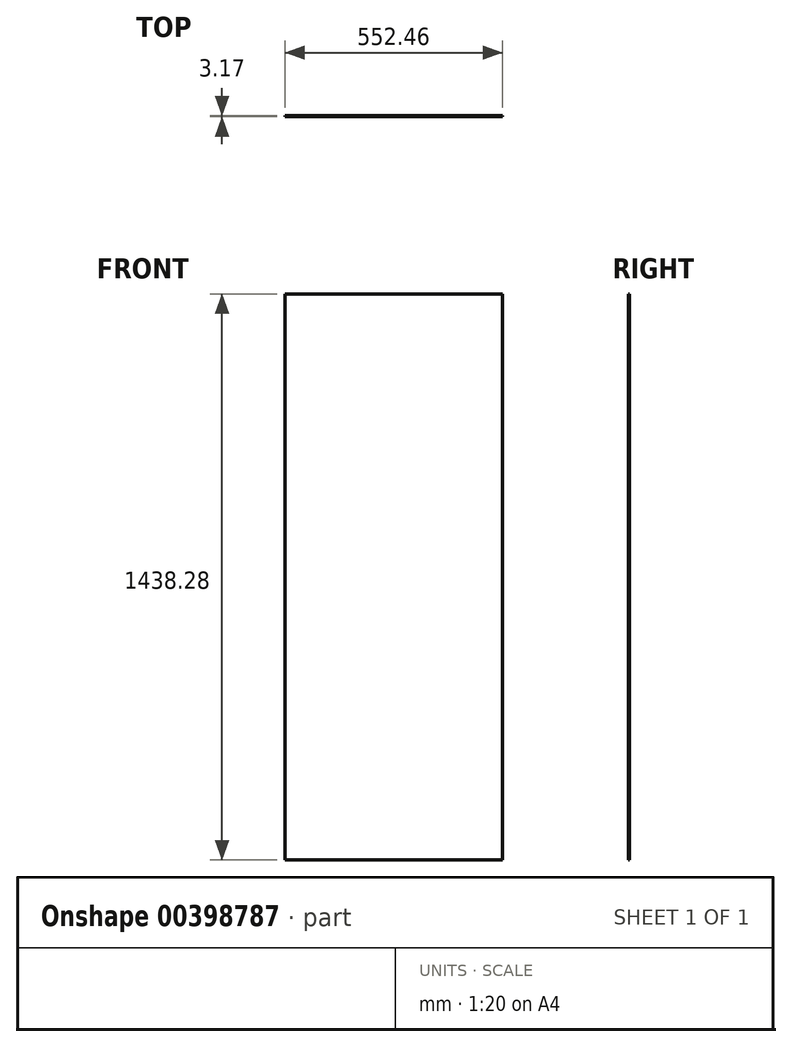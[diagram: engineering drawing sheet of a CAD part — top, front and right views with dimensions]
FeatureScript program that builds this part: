
annotation { "Feature Type Name" : "Feature", "Feature Type Description" : "" }
export const myFeature = defineFeature(function(context is Context, id is Id, definition is map)
    precondition{}
    {
        {
            var Q0;
            Q0=qCreatedBy(makeId("Front.planeOp"),FACE);
            var sketch = newSketch(context, id + "F0", { "sketchPlane" : qUnion([Q0])});
            skLineSegment(sketch, "E0.bottom", {"start": v(276.23, 719.14) * mm, "end": v(-276.23, 719.14) * mm});
            skLineSegment(sketch, "E0.top", {"start": v(276.23, -719.14) * mm, "end": v(-276.23, -719.14) * mm});
            skLineSegment(sketch, "E0.left", {"start": v(276.23, 719.14) * mm, "end": v(276.23, -719.14) * mm});
            skLineSegment(sketch, "E0.right", {"start": v(-276.23, 719.14) * mm, "end": v(-276.23, -719.14) * mm});
            skPoint(sketch, "E0.middle", {"position": v(0, 0) * mm});
            skSolve(sketch);
        }
        {
            var Q0;
            Q0 = qSketchRegion(id + "F0", true);
            extrude(context, id + "F1", {"entities" : qUnion([Q0]), "depth" : 3.17 * mm});
        }
    });
